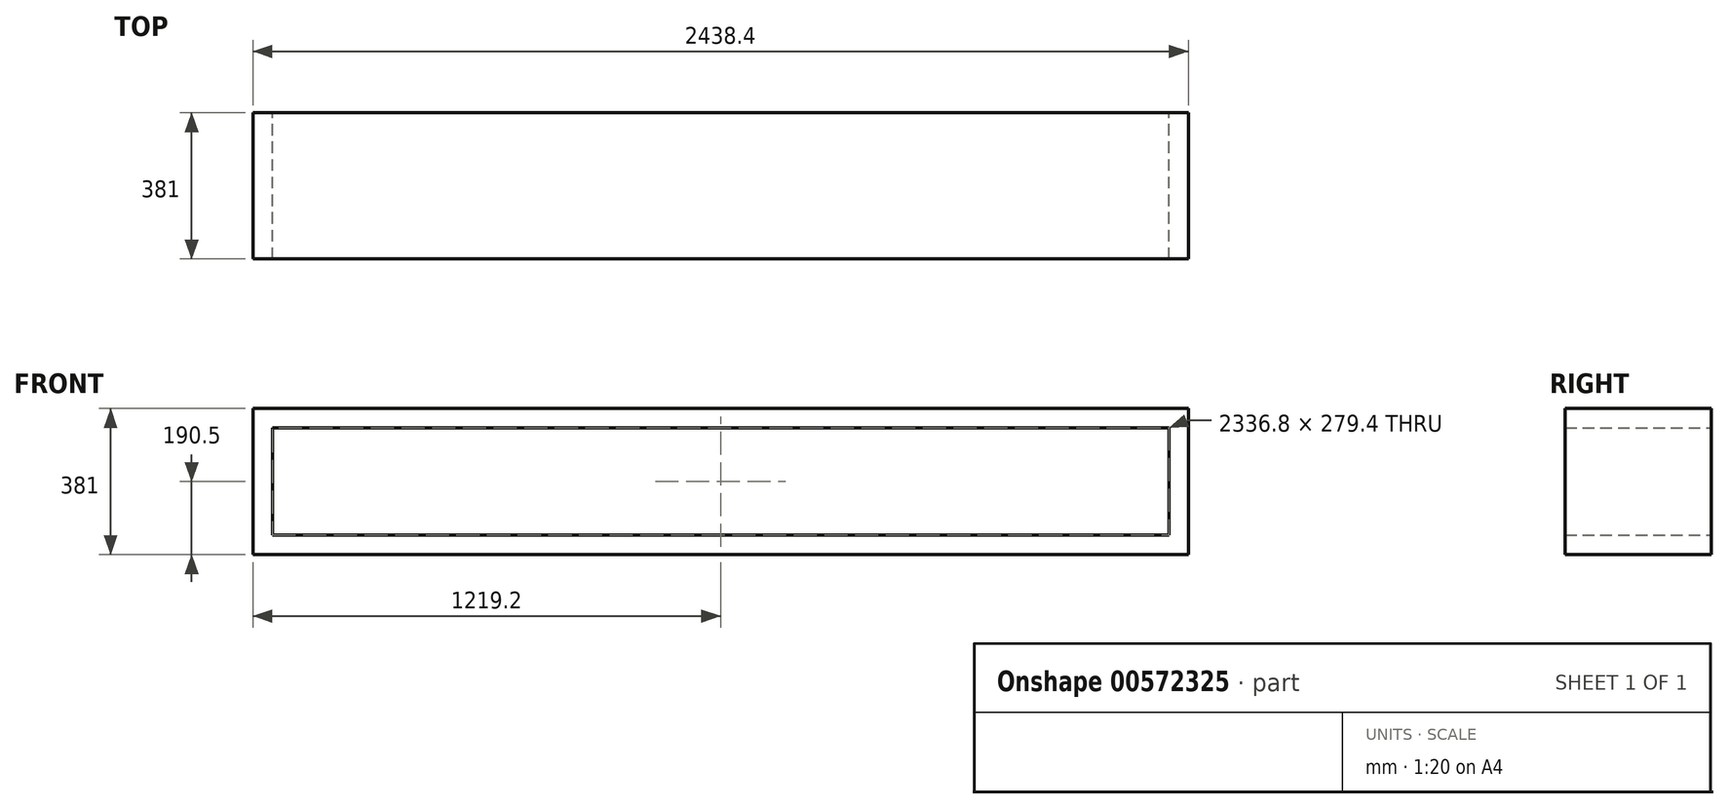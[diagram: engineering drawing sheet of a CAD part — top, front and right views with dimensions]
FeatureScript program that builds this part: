
annotation { "Feature Type Name" : "Feature", "Feature Type Description" : "" }
export const myFeature = defineFeature(function(context is Context, id is Id, definition is map)
    precondition{}
    {
        {
            var Q0;
            Q0=qCreatedBy(makeId("Front.planeOp"),FACE);
            var sketch = newSketch(context, id + "F0", { "sketchPlane" : qUnion([Q0])});
            skLineSegment(sketch, "E0.bottom", {"start": v(0, 0) * mm, "end": v(2438.4, 0) * mm});
            skLineSegment(sketch, "E0.top", {"start": v(0, 381) * mm, "end": v(2438.4, 381) * mm});
            skLineSegment(sketch, "E0.left", {"start": v(0, 0) * mm, "end": v(0, 381) * mm});
            skLineSegment(sketch, "E0.right", {"start": v(2438.4, 0) * mm, "end": v(2438.4, 381) * mm});
            skLineSegment(sketch, "E1.0", {"start": v(50.8, 330.2) * mm, "end": v(2387.6, 330.2) * mm});
            skLineSegment(sketch, "E1.1", {"start": v(50.8, 50.8) * mm, "end": v(50.8, 330.2) * mm});
            skLineSegment(sketch, "E1.2", {"start": v(50.8, 50.8) * mm, "end": v(2387.6, 50.8) * mm});
            skLineSegment(sketch, "E1.3", {"start": v(2387.6, 50.8) * mm, "end": v(2387.6, 330.2) * mm});
            skLineSegment(sketch, "E2", {"start": v(2387.6, 330.2) * mm, "end": v(2438.4, 381) * mm});
            skLineSegment(sketch, "E3", {"start": v(2387.6, 50.8) * mm, "end": v(2438.4, 0) * mm});
            skLineSegment(sketch, "E4", {"start": v(50.8, 330.2) * mm, "end": v(0, 381) * mm});
            skLineSegment(sketch, "E5", {"start": v(50.8, 50.8) * mm, "end": v(0, 0) * mm});
            skLineSegment(sketch, "E6.bottom", {"start": v(762, 330.2) * mm, "end": v(812.8, 330.2) * mm});
            skLineSegment(sketch, "E6.top", {"start": v(762, 50.8) * mm, "end": v(812.8, 50.8) * mm});
            skLineSegment(sketch, "E6.left", {"start": v(762, 330.2) * mm, "end": v(762, 50.8) * mm});
            skLineSegment(sketch, "E6.right", {"start": v(812.8, 330.2) * mm, "end": v(812.8, 50.8) * mm});
            skLineSegment(sketch, "E7.bottom", {"start": v(1625.6, 330.2) * mm, "end": v(1676.4, 330.2) * mm});
            skLineSegment(sketch, "E7.top", {"start": v(1625.6, 50.8) * mm, "end": v(1676.4, 50.8) * mm});
            skLineSegment(sketch, "E7.left", {"start": v(1625.6, 330.2) * mm, "end": v(1625.6, 50.8) * mm});
            skLineSegment(sketch, "E7.right", {"start": v(1676.4, 330.2) * mm, "end": v(1676.4, 50.8) * mm});
            skSolve(sketch);
        }
        {
            var Q0;
            Q0=makeQuery(id+"F0.imprint","IMPRINT",FACE,{"disambiguationData":[TD([[makeQuery(id+"F0.imprint","IMPRINT",EDGE,{"derivedFrom":sQuery(id+"F0.wireOp",EDGE,"E0.bottom")}),1.0]])]});
            var Q1;
            Q1=makeQuery(id+"F0.imprint","IMPRINT",FACE,{"disambiguationData":[TD([[makeQuery(id+"F0.imprint","IMPRINT",EDGE,{"derivedFrom":sQuery(id+"F0.wireOp",EDGE,"E0.left")}),-1.0]])]});
            var Q2;
            Q2=makeQuery(id+"F0.imprint","IMPRINT",FACE,{"disambiguationData":[TD([[makeQuery(id+"F0.imprint","IMPRINT",EDGE,{"derivedFrom":sQuery(id+"F0.wireOp",EDGE,"E0.right")}),1.0]])]});
            var Q3;
            Q3=makeQuery(id+"F0.imprint","IMPRINT",FACE,{"disambiguationData":[TD([[makeQuery(id+"F0.imprint","IMPRINT",EDGE,{"derivedFrom":sQuery(id+"F0.wireOp",EDGE,"E0.top")}),-1.0]])]});
            extrude(context, id + "F1", {"entities" : qUnion([Q0, Q1, Q2, Q3]), "depth" : 381 * mm, "offsetDistance" : 25.4 * mm});
        }
        {
            var Q0;
            Q0 = qSketchRegion(id + "F0", true);
            var Q1;
            Q1=makeQuery(id+"F0.imprint","IMPRINT",FACE,{"disambiguationData":[TD([[makeQuery(id+"F0.imprint","IMPRINT",EDGE,{"derivedFrom":sQuery(id+"F0.wireOp",EDGE,"E6.bottom")}),-1.0]])]});
            var Q2;
            Q2=makeQuery(id+"F0.imprint","IMPRINT",FACE,{"disambiguationData":[TD([[makeQuery(id+"F0.imprint","IMPRINT",EDGE,{"derivedFrom":sQuery(id+"F0.wireOp",EDGE,"E7.bottom")}),-1.0]])]});
            extrude(context, id + "F2", {"entities" : qUnion([Q0, Q1, Q2]), "operationType" : NewBodyOperationType.ADD, "depth" : 381 * mm, "offsetDistance" : 25.4 * mm});
        }
    });
